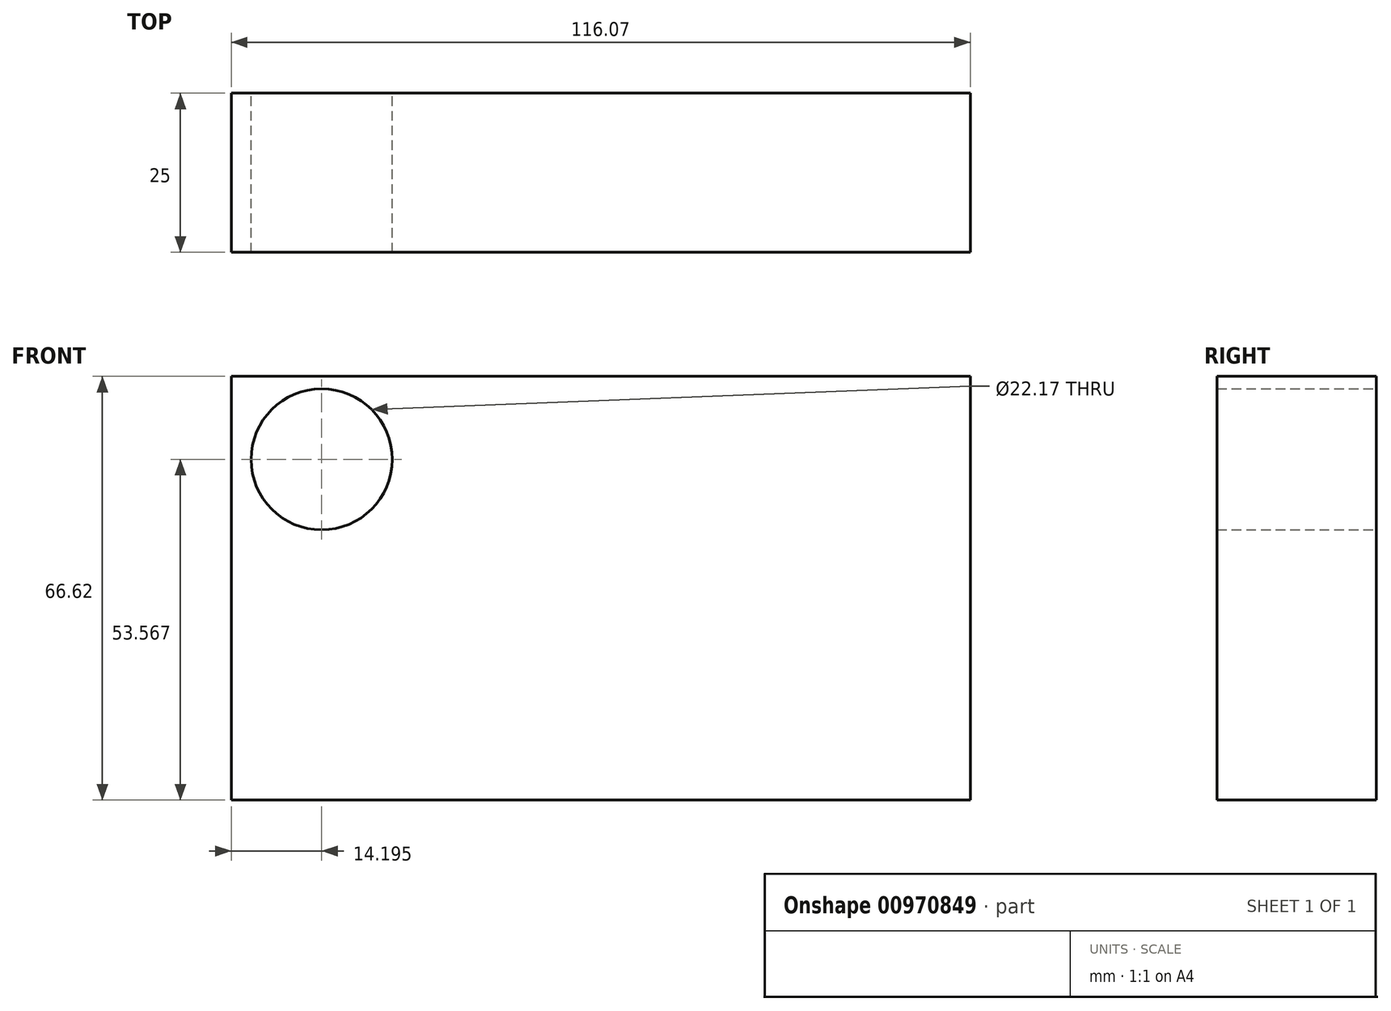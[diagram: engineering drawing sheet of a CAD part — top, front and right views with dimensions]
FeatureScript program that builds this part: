
annotation { "Feature Type Name" : "Feature", "Feature Type Description" : "" }
export const myFeature = defineFeature(function(context is Context, id is Id, definition is map)
    precondition{}
    {
        {
            var Q0;
            Q0=qCreatedBy(makeId("Front.planeOp"),FACE);
            var sketch = newSketch(context, id + "F0", { "sketchPlane" : qUnion([Q0])});
            skLineSegment(sketch, "E0.bottom", {"start": v(-61.58, 38.12) * mm, "end": v(54.49, 38.12) * mm});
            skLineSegment(sketch, "E0.top", {"start": v(-61.58, -28.5) * mm, "end": v(54.49, -28.5) * mm});
            skLineSegment(sketch, "E0.left", {"start": v(-61.58, 38.12) * mm, "end": v(-61.58, -28.5) * mm});
            skLineSegment(sketch, "E0.right", {"start": v(54.49, 38.12) * mm, "end": v(54.49, -28.5) * mm});
            skCircle(sketch, "E1", {"center": v(-47.38, 25.07) * mm, "radius": 11.08 * mm});
            skSolve(sketch);
        }
        {
            var Q0;
            Q0=makeQuery(id+"F0.imprint","IMPRINT",FACE,{"disambiguationData":[TD([[makeQuery(id+"F0.imprint","IMPRINT",EDGE,{"derivedFrom":sQuery(id+"F0.wireOp",EDGE,"E0.bottom")}),-1.0]])]});
            extrude(context, id + "F1", {"entities" : qUnion([Q0]), "depth" : 25 * mm, "offsetDistance" : 25 * mm});
        }
    });
